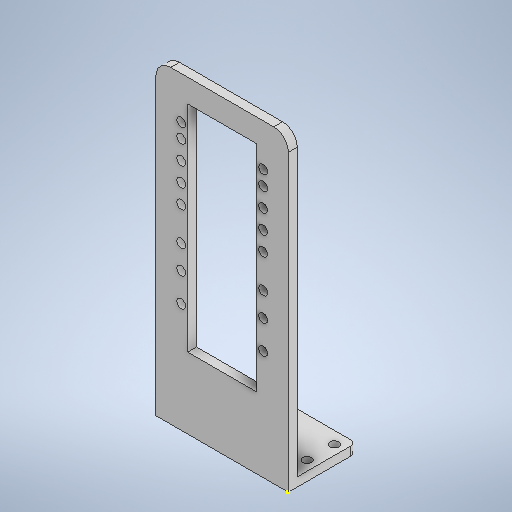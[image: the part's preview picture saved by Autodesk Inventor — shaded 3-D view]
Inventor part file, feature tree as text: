
AUTODESK INVENTOR PART (.ipt)
format: ipt  version: 2025.1 (Build 291241020, 241B)  size: 359,424 bytes
history: native  units: mm
features: extrude x6, sketch x3, fillet x3
ambient origin geometry x8: Origin, YZ Plane, XZ Plane, XY Plane, X Axis, Y Axis, Z Axis, Center Point
bodies: Solid1 (feature_tree)
feature tree (12):
  sketch  "Sketch1"  dims[d0=45.0mm d1=20.0mm]
  extrude  "Extrusion1"  Depth=20.0mm
  extrude  "Extrusion2"  Depth=3.0mm
  sketch  "Sketch2"  dims[d2=3.0mm d3=0.0mm d4=3.0mm]
  extrude  "Extrusion3"  Depth=3.0mm
  extrude  "Extrusion4"  Depth=3.0mm
  extrude  "Extrusion5"  TaperAngle=0.0deg  [1 undecoded]
  extrude  "Extrusion6"  Depth=105.0mm
  fillet  "Fillet1"  Radius=3.0mm
  fillet  "Fillet2"  Radius=45.0mm
  fillet  "Fillet3"  Radius=23.436mm
  sketch  "Sketch4"  dims[d5=3.0mm d6=3.0mm d7=3.0mm d8=0.0mm d9=0.0mm d10=105.0mm d11=3.0mm d12=0.0mm d13=45.0mm d14=23.436mm d15=12.9mm d17=10.782mm d18=3.0mm d19=3.0mm d20=2.2mm d21=2.2mm d22=23.436mm d23=12.9mm d24=3.0mm d25=3.0mm d26=2.2mm d27=2.2mm d28=23.436mm d29=12.9mm d30=3.0mm d31=3.0mm d32=2.2mm d33=2.2mm d34=23.436mm d35=12.9mm d36=3.0mm d37=3.0mm d38=2.2mm d39=2.2mm d40=0.0mm d41=0.0mm d42=3.0mm d43=0.0mm d44=3.0mm d45=3.0mm d46=3.0mm d47=3.0mm d48=3.0mm d49=3.0mm d50=3.0mm d51=3.0mm d52=3.0mm d53=0.0mm d54=5.0mm d55=5.0mm d56=2.0mm d16=0.872665mm]
note: 1 required parameter value undecoded (feature->parameter linkage not recoverable at this tier; creation-order binding heuristic only, values carry confidence <= 0.55)
